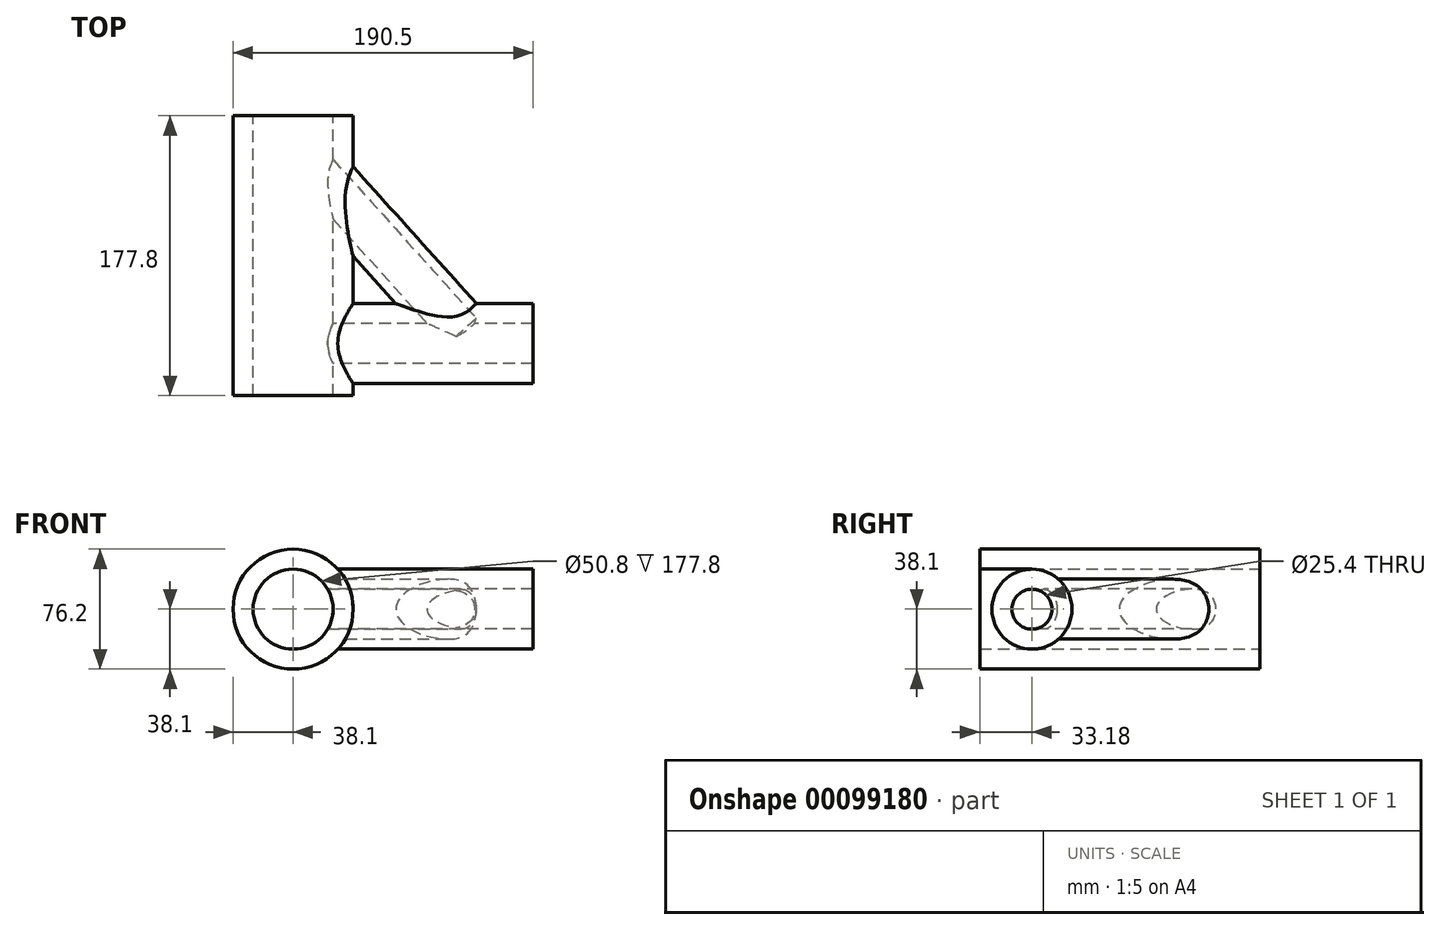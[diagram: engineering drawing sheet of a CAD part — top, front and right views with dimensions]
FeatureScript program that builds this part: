
annotation { "Feature Type Name" : "Feature", "Feature Type Description" : "" }
export const myFeature = defineFeature(function(context is Context, id is Id, definition is map)
    precondition{}
    {
        {
            var Q0;
            Q0=qCreatedBy(makeId("Front.planeOp"),FACE);
            var sketch = newSketch(context, id + "F0", { "sketchPlane" : qUnion([Q0])});
            skCircle(sketch, "E0", {"center": v(0, 0) * mm, "radius": 25.4 * mm});
            skCircle(sketch, "E1", {"center": v(0, 0) * mm, "radius": 38.1 * mm});
            skSolve(sketch);
        }
        {
            var Q0;
            Q0=makeQuery(id+"F0.imprint","IMPRINT",FACE,{"disambiguationData":[TD([[makeQuery(id+"F0.imprint","IMPRINT",EDGE,{"derivedFrom":sQuery(id+"F0.wireOp",EDGE,"E0")}),-1.0]])]});
            extrude(context, id + "F1", {"entities" : qUnion([Q0]), "depth" : 177.8 * mm});
        }
        {
            var Q0;
            Q0=qCreatedBy(makeId("Top.planeOp"),FACE);
            var sketch = newSketch(context, id + "F2", { "sketchPlane" : qUnion([Q0])});
            skLineSegment(sketch, "E2", {"start": v(108.76, -135.77) * mm, "end": v(0, -15.07) * mm, "construction": true});
            skSolve(sketch);
        }
        {
            var Q0;
            Q0=sQuery(id+"F2.wireOp",EDGE,"E2");
            cPlane(context, id + "F3", {"entities" : qUnion([Q0]), "cplaneType" : CPlaneType.MID_PLANE, "offset" : 152.4 * mm, "width" : 152.4 * mm, "height" : 152.4 * mm});
        }
        {
            var Q0;
            Q0=qCreatedBy(id+"F3.planeOp",FACE);
            var sketch = newSketch(context, id + "F4", { "sketchPlane" : qUnion([Q0])});
            skCircle(sketch, "E3", {"center": v(12.4, 0) * mm, "radius": 19.05 * mm});
            skCircle(sketch, "E4", {"center": v(12.4, 0) * mm, "radius": 12.7 * mm});
            skSolve(sketch);
        }
        {
            var Q0;
            Q0 = qSketchRegion(id + "F4", true);
            extrude(context, id + "F5", {"entities" : qUnion([Q0]), "operationType" : NewBodyOperationType.ADD, "depth" : 55.88 * mm, "hasSecondDirection" : true, "secondDirectionOppositeDirection" : true, "secondDirectionDepth" : 101.6 * mm});
        }
        {
            var Q0;
            Q0=qCreatedBy(makeId("Right.planeOp"),FACE);
            var sketch = newSketch(context, id + "F6", { "sketchPlane" : qUnion([Q0])});
            skCircle(sketch, "E5", {"center": v(-144.62, 0) * mm, "radius": 12.7 * mm});
            skCircle(sketch, "E6", {"center": v(-144.62, 0) * mm, "radius": 25.4 * mm});
            skSolve(sketch);
        }
        {
            var Q0;
            Q0 = qSketchRegion(id + "F6", true);
            extrude(context, id + "F7", {"entities" : qUnion([Q0]), "operationType" : NewBodyOperationType.ADD, "depth" : 152.4 * mm, "hasSecondDirection" : true, "secondDirectionOppositeDirection" : false, "secondDirectionDepth" : 25.4 * mm});
        }
        {
            var Q0;
            Q0=sQuery(id+"F6.wireOp",VERTEX,"E5.center");
            var Q1;
            Q1=makeQuery(id+"F1.opExtrude","SWEPT_BODY",BODY,{"disambiguationData":[OSD([sQuery(id+"F0.wireOp",EDGE,"E0"),sQuery(id+"F0.wireOp",EDGE,"E1")])]});
            hole(context, id + "F8", {"style" : HoleStyle.SIMPLE, "endStyle" : HoleEndStyle.BLIND, "oppositeDirection" : true, "holeDiameter" : 25.4 * mm, "holeDepth" : 127 * mm, "locations" : qUnion([Q0]), "scope" : qUnion([Q1])});
        }
        {
            var Q0;
            Q0=sQuery(id+"F0.wireOp",VERTEX,"E0.center");
            var Q1;
            Q1=makeQuery(id+"F1.opExtrude","SWEPT_BODY",BODY,{"disambiguationData":[OSD([sQuery(id+"F0.wireOp",EDGE,"E0"),sQuery(id+"F0.wireOp",EDGE,"E1")])]});
            hole(context, id + "F9", {"style" : HoleStyle.SIMPLE, "endStyle" : HoleEndStyle.BLIND, "oppositeDirection" : true, "holeDiameter" : 50.8 * mm, "holeDepth" : 177.8 * mm, "locations" : qUnion([Q0]), "scope" : qUnion([Q1])});
        }
        {
            var Q0;
            Q0=sQuery(id+"F4.wireOp",VERTEX,"E3.center");
            var Q1;
            Q1=makeQuery(id+"F1.opExtrude","SWEPT_BODY",BODY,{"disambiguationData":[OSD([sQuery(id+"F0.wireOp",EDGE,"E0"),sQuery(id+"F0.wireOp",EDGE,"E1")])]});
            hole(context, id + "F10", {"style" : HoleStyle.SIMPLE, "endStyle" : HoleEndStyle.BLIND, "oppositeDirection" : true, "holeDiameter" : 25.4 * mm, "holeDepth" : 50.8 * mm, "locations" : qUnion([Q0]), "scope" : qUnion([Q1])});
        }
        {
            var Q0;
            Q0=sQuery(id+"F4.wireOp",VERTEX,"E3.center");
            var Q1;
            Q1=makeQuery(id+"F1.opExtrude","SWEPT_BODY",BODY,{"disambiguationData":[OSD([sQuery(id+"F0.wireOp",EDGE,"E0"),sQuery(id+"F0.wireOp",EDGE,"E1")])]});
            hole(context, id + "F11", {"style" : HoleStyle.SIMPLE, "endStyle" : HoleEndStyle.BLIND, "holeDiameter" : 25.4 * mm, "holeDepth" : 12.7 * mm, "locations" : qUnion([Q0]), "scope" : qUnion([Q1])});
        }
    });
